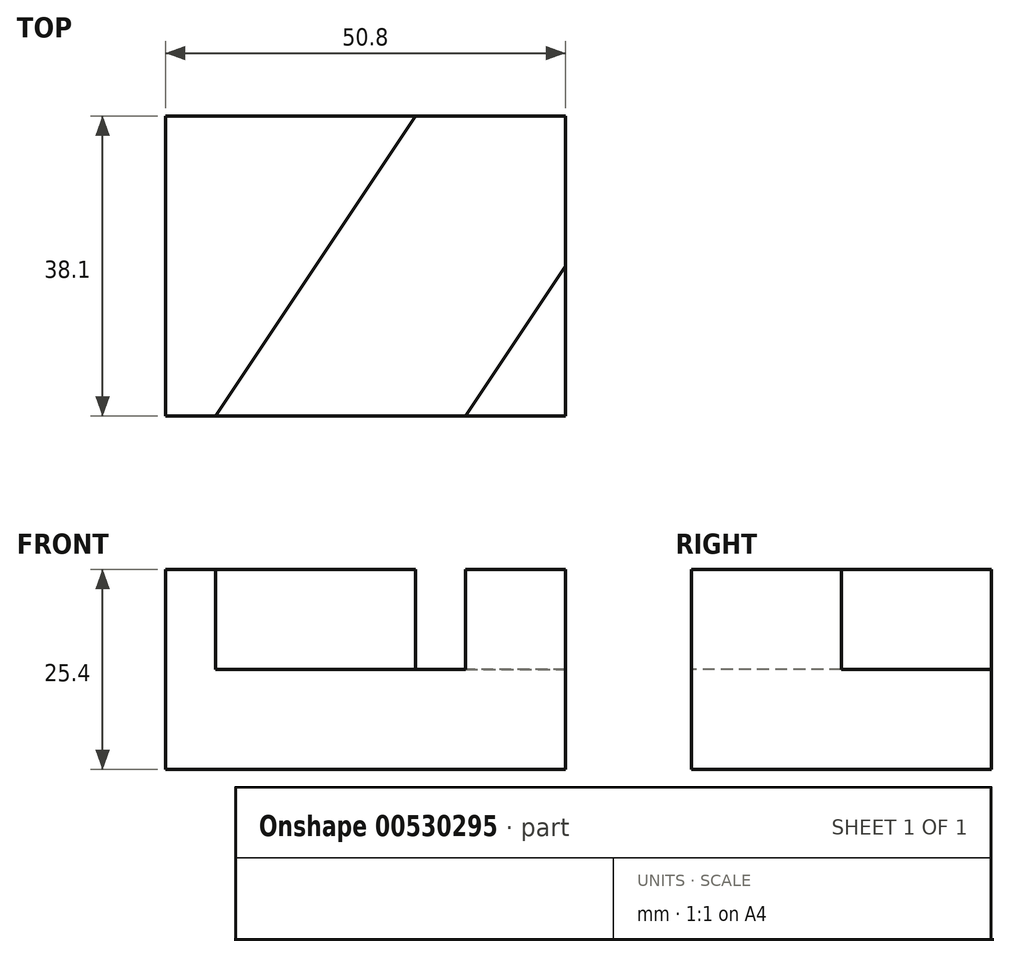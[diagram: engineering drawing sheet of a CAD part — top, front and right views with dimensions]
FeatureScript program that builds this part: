
annotation { "Feature Type Name" : "Feature", "Feature Type Description" : "" }
export const myFeature = defineFeature(function(context is Context, id is Id, definition is map)
    precondition{}
    {
        {
            var Q0;
            Q0=qCreatedBy(makeId("Front.planeOp"),FACE);
            var sketch = newSketch(context, id + "F0", { "sketchPlane" : qUnion([Q0])});
            skLineSegment(sketch, "E0", {"start": v(-25.67, 25.4) * mm, "end": v(-25.67, 0) * mm});
            skLineSegment(sketch, "E1", {"start": v(-25.67, 0) * mm, "end": v(25.13, 0) * mm});
            skLineSegment(sketch, "E2", {"start": v(25.13, 0) * mm, "end": v(25.13, 25.4) * mm});
            skLineSegment(sketch, "E3", {"start": v(25.13, 25.4) * mm, "end": v(-25.67, 25.4) * mm});
            skSolve(sketch);
        }
        {
            var Q0;
            Q0=makeQuery(id+"F0.imprint","IMPRINT",FACE,{"disambiguationData":[TD([[makeQuery(id+"F0.imprint","IMPRINT",EDGE,{"derivedFrom":sQuery(id+"F0.wireOp",EDGE,"E0")}),1.0]])]});
            extrude(context, id + "F1", {"entities" : qUnion([Q0]), "depth" : 38.1 * mm, "offsetDistance" : 25.4 * mm});
        }
        {
            var Q0;
            Q0=makeQuery(id+"F1.opExtrude","SWEPT_FACE",FACE,{"disambiguationData":[OSD([sQuery(id+"F0.wireOp",EDGE,"E3")])]});
            var sketch = newSketch(context, id + "F2", { "sketchPlane" : qUnion([Q0])});
            skLineSegment(sketch, "E4", {"start": v(6.08, 0) * mm, "end": v(-19.32, -38.1) * mm});
            skLineSegment(sketch, "E5", {"start": v(12.43, -38.1) * mm, "end": v(25.13, -19.05) * mm});
            skSolve(sketch);
        }
        {
            var Q0;
            {var subQ5=sQuery(id+"F2.wireOp",EDGE,"E4");Q0=makeQuery(id+"F2.imprint","IMPRINT",FACE,{"disambiguationData":[TD([[makeQuery(id+"F2.imprint","IMPRINT",EDGE,{"derivedFrom":subQ5}),1.0]])]});}
            extrude(context, id + "F3", {"entities" : qUnion([Q0]), "operationType" : NewBodyOperationType.REMOVE, "oppositeDirection" : true, "depth" : 12.7 * mm, "offsetDistance" : 25.4 * mm});
        }
    });
